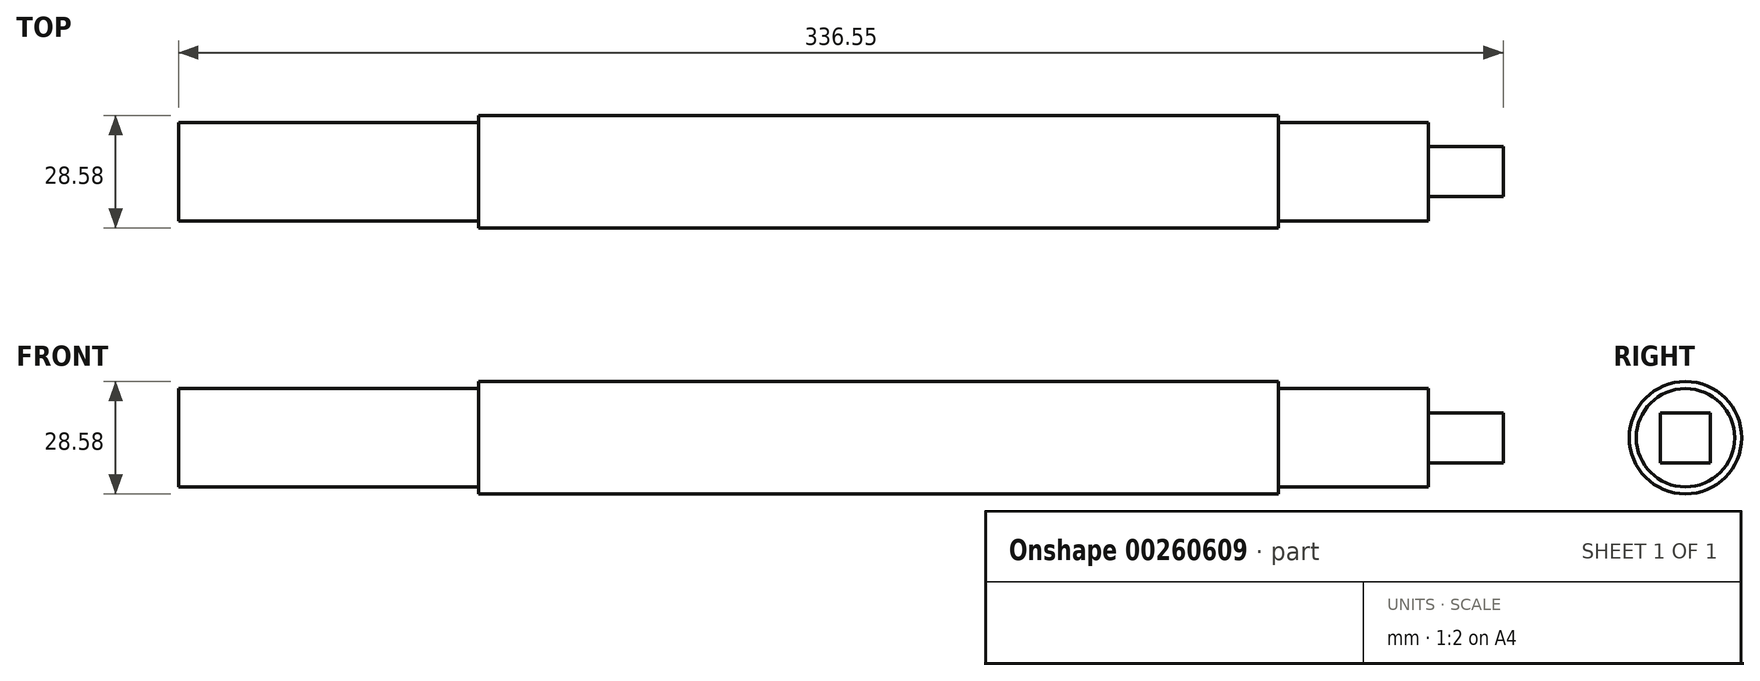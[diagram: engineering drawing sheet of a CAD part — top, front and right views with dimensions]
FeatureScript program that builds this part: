
annotation { "Feature Type Name" : "Feature", "Feature Type Description" : "" }
export const myFeature = defineFeature(function(context is Context, id is Id, definition is map)
    precondition{}
    {
        {
            var Q0;
            Q0=qCreatedBy(makeId("Right.planeOp"),FACE);
            var sketch = newSketch(context, id + "F0", { "sketchPlane" : qUnion([Q0])});
            skCircle(sketch, "E0", {"center": v(0, 0) * mm, "radius": 14.29 * mm});
            skCircle(sketch, "E1", {"center": v(0, 0) * mm, "radius": 12.5 * mm});
            skLineSegment(sketch, "E2.bottom", {"start": v(6.35, 6.35) * mm, "end": v(-6.35, 6.35) * mm});
            skLineSegment(sketch, "E2.top", {"start": v(6.35, -6.35) * mm, "end": v(-6.35, -6.35) * mm});
            skLineSegment(sketch, "E2.left", {"start": v(6.35, 6.35) * mm, "end": v(6.35, -6.35) * mm});
            skLineSegment(sketch, "E2.right", {"start": v(-6.35, 6.35) * mm, "end": v(-6.35, -6.35) * mm});
            skSolve(sketch);
        }
        {
            var Q0;
            Q0=makeQuery(id+"F0.imprint","IMPRINT",FACE,{"disambiguationData":[TD([[makeQuery(id+"F0.imprint","IMPRINT",EDGE,{"derivedFrom":sQuery(id+"F0.wireOp",EDGE,"E0")}),1.0]])]});
            extrude(context, id + "F1", {"entities" : qUnion([Q0]), "depth" : 101.6 * mm, "hasSecondDirection" : true, "secondDirectionOppositeDirection" : true, "secondDirectionDepth" : 101.6 * mm});
        }
        {
            var Q0;
            Q0=makeQuery(id+"F0.imprint","IMPRINT",FACE,{"disambiguationData":[TD([[makeQuery(id+"F0.imprint","IMPRINT",EDGE,{"derivedFrom":sQuery(id+"F0.wireOp",EDGE,"E1")}),1.0]])]});
            extrude(context, id + "F2", {"entities" : qUnion([Q0]), "operationType" : NewBodyOperationType.ADD, "depth" : 139.7 * mm, "hasSecondDirection" : true, "secondDirectionOppositeDirection" : true, "secondDirectionDepth" : 177.8 * mm});
        }
        {
            var Q0;
            Q0=makeQuery(id+"F0.imprint","IMPRINT",FACE,{"disambiguationData":[TD([[makeQuery(id+"F0.imprint","IMPRINT",EDGE,{"derivedFrom":sQuery(id+"F0.wireOp",EDGE,"E2.bottom")}),1.0]])]});
            var Q1;
            Q1=makeQuery(id+"F2.opExtrude","CAP_FACE",FACE,{"disambiguationData":[OSD([sQuery(id+"F0.wireOp",EDGE,"E1"),sQuery(id+"F0.wireOp",EDGE,"E2.bottom"),sQuery(id+"F0.wireOp",EDGE,"E2.top"),sQuery(id+"F0.wireOp",EDGE,"E2.left"),sQuery(id+"F0.wireOp",EDGE,"E2.right")])],"isStart":true});
            extrude(context, id + "F3", {"entities" : qUnion([Q0]), "operationType" : NewBodyOperationType.ADD, "depth" : 158.75 * mm, "hasSecondDirection" : true, "secondDirectionBound" : SecondDirectionBoundingType.UP_TO_SURFACE, "secondDirectionOppositeDirection" : true, "secondDirectionBoundEntityFace" : qUnion([Q1]), "secondDirectionDepth" : 25.4 * mm});
        }
    });
